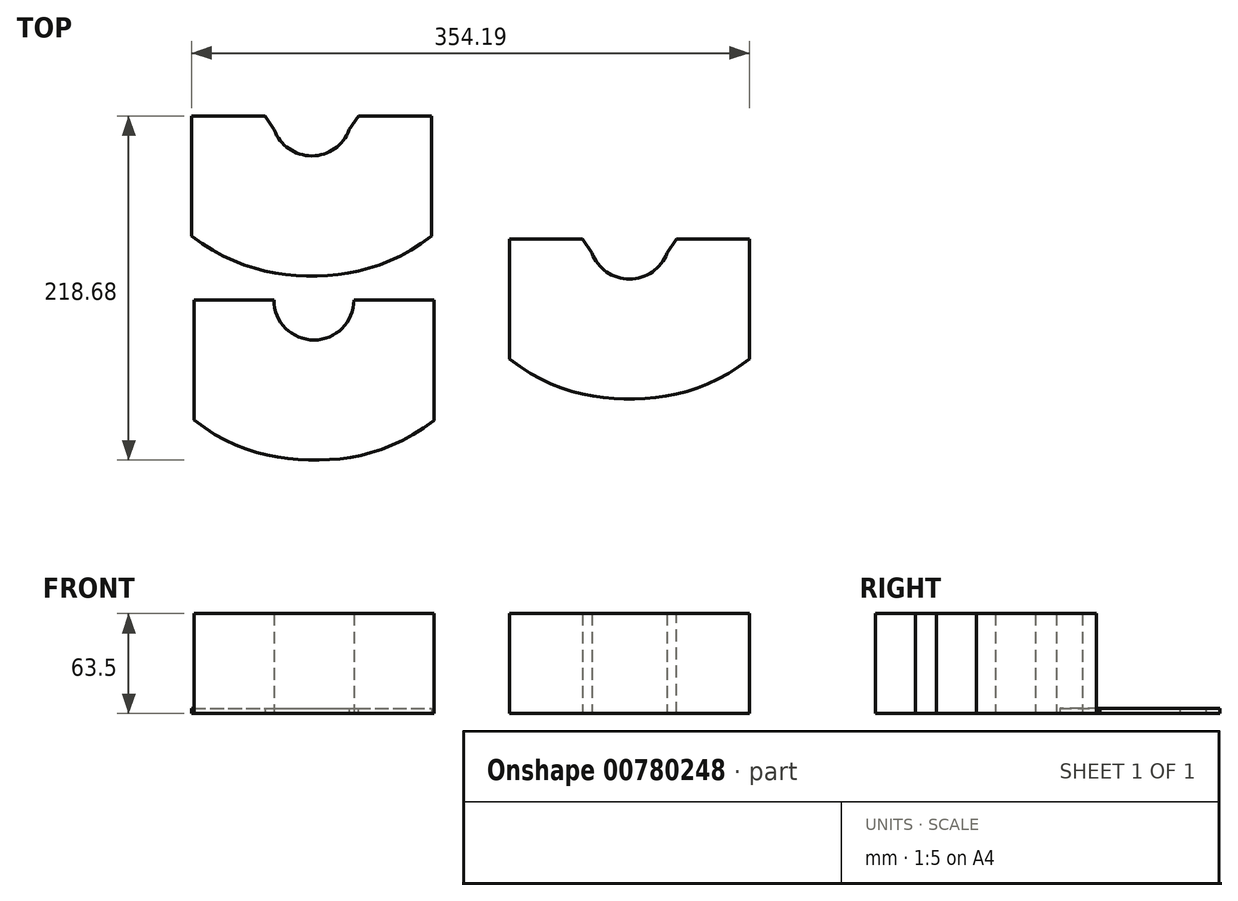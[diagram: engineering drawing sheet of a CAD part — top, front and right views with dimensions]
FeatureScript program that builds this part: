
annotation { "Feature Type Name" : "Feature", "Feature Type Description" : "" }
export const myFeature = defineFeature(function(context is Context, id is Id, definition is map)
    precondition{}
    {
        {
            var Q0;
            Q0=qCreatedBy(makeId("Top.planeOp"),FACE);
            var sketch = newSketch(context, id + "F0", { "sketchPlane" : qUnion([Q0])});
            skLineSegment(sketch, "E0.bottom", {"start": v(-76.2, 25.4) * mm, "end": v(-50.8, 25.4) * mm});
            skLineSegment(sketch, "E0.top", {"start": v(-70.9, -50.8) * mm, "end": v(-50.8, -50.8) * mm});
            skLineSegment(sketch, "E0.left", {"start": v(-76.2, 25.4) * mm, "end": v(-76.2, -50.8) * mm});
            skLineSegment(sketch, "E0.right", {"start": v(-50.8, 22.22) * mm, "end": v(-50.8, -50.8) * mm});
            skLineSegment(sketch, "E1.bottom", {"start": v(50.8, 25.4) * mm, "end": v(76.2, 25.4) * mm});
            skLineSegment(sketch, "E1.top", {"start": v(50.8, -50.98) * mm, "end": v(70.9, -50.98) * mm});
            skLineSegment(sketch, "E1.left", {"start": v(50.8, 22.22) * mm, "end": v(50.8, -50.98) * mm});
            skLineSegment(sketch, "E1.right", {"start": v(76.2, 25.4) * mm, "end": v(76.2, -50.98) * mm});
            skLineSegment(sketch, "E2.bottom", {"start": v(-50.8, 25.4) * mm, "end": v(-25.4, 25.4) * mm});
            skLineSegment(sketch, "E2.top", {"start": v(-50.8, 0) * mm, "end": v(-28.57, 0) * mm});
            skLineSegment(sketch, "E2.left", {"start": v(-50.8, 22.22) * mm, "end": v(-50.8, 0) * mm});
            skLineSegment(sketch, "E2.right", {"start": v(-25.4, 25.4) * mm, "end": v(-25.4, 25.4) * mm});
            skLineSegment(sketch, "E3.bottom", {"start": v(50.8, 25.4) * mm, "end": v(25.4, 25.4) * mm});
            skLineSegment(sketch, "E3.top", {"start": v(50.8, 0) * mm, "end": v(28.58, 0) * mm});
            skLineSegment(sketch, "E3.left", {"start": v(50.8, 22.22) * mm, "end": v(50.8, 0) * mm});
            skLineSegment(sketch, "E3.right", {"start": v(25.4, 25.4) * mm, "end": v(25.4, 25.4) * mm});
            skLineSegment(sketch, "E4", {"start": v(0, 0) * mm, "end": v(0, 0) * mm});
            skLineSegment(sketch, "E5", {"start": v(-50.8, -50.8) * mm, "end": v(50.8, -50.98) * mm, "construction": true});
            skFitSpline(sketch, "E6", {"points": [v(-76.2, -50.8) * mm, v(0, -76.3) * mm, v(76.2, -50.98) * mm], "startDerivative": vector(152.37, -117.67) * mm, "endDerivative": vector(152.4, 117.72) * mm});
            skLineSegment(sketch, "E7", {"start": v(0, -50.9) * mm, "end": v(0, -76.3) * mm, "construction": true});
            skLineSegment(sketch, "E8", {"start": v(50.8, -50.98) * mm, "end": v(50.8, -70.6) * mm, "construction": true});
            skLineSegment(sketch, "E9", {"start": v(-50.8, -50.8) * mm, "end": v(-50.8, -70.42) * mm, "construction": true});
            skLineSegment(sketch, "E10.0", {"start": v(-73.02, 22.23) * mm, "end": v(-50.8, 22.23) * mm});
            skLineSegment(sketch, "E10.1", {"start": v(-50.8, 22.23) * mm, "end": v(-28.57, 22.23) * mm});
            skLineSegment(sketch, "E10.2", {"start": v(-73.02, 22.22) * mm, "end": v(-73.02, -49.23) * mm});
            skLineSegment(sketch, "E10.3", {"start": v(-28.57, 22.22) * mm, "end": v(-28.57, 22.22) * mm});
            skLineSegment(sketch, "E10.4", {"start": v(-3.17, -3.17) * mm, "end": v(3.18, -3.17) * mm});
            skLineSegment(sketch, "E10.5", {"start": v(28.58, 22.22) * mm, "end": v(28.58, 22.23) * mm});
            skFitSpline(sketch, "E10.6", {"points": [v(-74.26, -48.29) * mm, v(-68.05, -53.08) * mm, v(-55.68, -60.96) * mm, v(-40.26, -67.2) * mm, v(-27.92, -70.4) * mm, v(-18.64, -72.02) * mm, v(-10.9, -72.77) * mm, v(-4.68, -73.06) * mm, v(0, -73.14) * mm, v(4.66, -73.08) * mm, v(10.88, -72.81) * mm, v(18.63, -72.09) * mm, v(27.9, -70.5) * mm, v(40.25, -67.33) * mm, v(55.67, -61.13) * mm, v(68.05, -53.27) * mm, v(74.26, -48.47) * mm]});
            skLineSegment(sketch, "E10.7", {"start": v(73.02, 22.22) * mm, "end": v(73.02, -49.41) * mm});
            skLineSegment(sketch, "E10.8", {"start": v(50.8, 22.23) * mm, "end": v(73.02, 22.23) * mm});
            skLineSegment(sketch, "E10.9", {"start": v(50.8, 22.23) * mm, "end": v(28.58, 22.23) * mm});
            skPoint(sketch, "E11.visualSharp", {"position": v(-25.4, 0) * mm});
            skArc(sketch, "E11.filletArc", {"start": v(-25.4, 25.4) * mm, "mid": v(-17.96, 7.44) * mm, "end": v(0, 0) * mm});
            skPoint(sketch, "E12.visualSharp", {"position": v(25.4, 0) * mm});
            skArc(sketch, "E12.filletArc", {"start": v(0, 0) * mm, "mid": v(17.96, 7.44) * mm, "end": v(25.4, 25.4) * mm});
            skPoint(sketch, "E13.visualSharp", {"position": v(-28.57, -3.18) * mm});
            skArc(sketch, "E13.filletArc", {"start": v(-28.57, 22.22) * mm, "mid": v(-21.14, 4.26) * mm, "end": v(-3.17, -3.18) * mm});
            skPoint(sketch, "E14.visualSharp", {"position": v(28.58, -3.18) * mm});
            skArc(sketch, "E14.filletArc", {"start": v(3.18, -3.17) * mm, "mid": v(21.14, 4.26) * mm, "end": v(28.58, 22.23) * mm});
            skSolve(sketch);
        }
        {
            var Q0;
            Q0=qCreatedBy(makeId("Top.planeOp"),FACE);
            var sketch = newSketch(context, id + "F1", { "sketchPlane" : qUnion([Q0])});
            skLineSegment(sketch, "E15.bottom", {"start": v(-77.6, 142.4) * mm, "end": v(-52.2, 142.4) * mm});
            skLineSegment(sketch, "E15.left", {"start": v(-77.6, 142.4) * mm, "end": v(-77.6, 66.2) * mm});
            skLineSegment(sketch, "E16.bottom", {"start": v(49.4, 142.4) * mm, "end": v(74.8, 142.4) * mm});
            skLineSegment(sketch, "E16.right", {"start": v(74.8, 142.4) * mm, "end": v(74.8, 66.2) * mm});
            skLineSegment(sketch, "E17.bottom", {"start": v(-52.2, 142.4) * mm, "end": v(-26.8, 142.4) * mm});
            skLineSegment(sketch, "E17.right", {"start": v(-26.8, 142.4) * mm, "end": v(-26.8, 142.4) * mm});
            skLineSegment(sketch, "E18.bottom", {"start": v(49.4, 142.4) * mm, "end": v(24, 142.4) * mm});
            skLineSegment(sketch, "E18.right", {"start": v(24, 142.4) * mm, "end": v(24, 142.4) * mm});
            skLineSegment(sketch, "E19", {"start": v(-1.4, 117) * mm, "end": v(-1.4, 117) * mm});
            skFitSpline(sketch, "E20", {"points": [v(-77.6, 66.2) * mm, v(-1.4, 40.8) * mm, v(74.8, 66.2) * mm], "startDerivative": vector(152.4, -117.7) * mm, "endDerivative": vector(152.4, 117.7) * mm});
            skPoint(sketch, "E21.visualSharp", {"position": v(-26.8, 117) * mm});
            skArc(sketch, "E21.filletArc", {"start": v(-26.8, 142.4) * mm, "mid": v(-19.36, 124.43) * mm, "end": v(-1.4, 117) * mm});
            skPoint(sketch, "E22.visualSharp", {"position": v(24, 117) * mm});
            skArc(sketch, "E22.filletArc", {"start": v(-1.4, 117) * mm, "mid": v(16.56, 124.43) * mm, "end": v(24, 142.4) * mm});
            skLineSegment(sketch, "E23", {"start": v(-26.8, 142.4) * mm, "end": v(24, 142.4) * mm, "construction": true});
            skSolve(sketch);
        }
        {
            var Q0;
            Q0=makeQuery(id+"F0.imprint","IMPRINT",FACE,{"disambiguationData":[TD([[makeQuery(id+"F0.imprint","IMPRINT",EDGE,{"derivedFrom":sQuery(id+"F0.wireOp",EDGE,"E0.bottom")}),-1.0]])]});
            extrude(context, id + "F2", {"entities" : qUnion([Q0]), "depth" : 63.5 * mm, "offsetDistance" : 25.4 * mm});
        }
        {
            var Q0;
            Q0=makeQuery(id+"F1.imprint","IMPRINT",FACE,{"disambiguationData":[TD([[makeQuery(id+"F1.imprint","IMPRINT",EDGE,{"derivedFrom":sQuery(id+"F1.wireOp",EDGE,"E15.bottom")}),-1.0]])]});
            extrude(context, id + "F3", {"entities" : qUnion([Q0]), "depth" : 3.17 * mm, "offsetDistance" : 25.4 * mm});
        }
        {
            var Q0;
            Q0=makeQuery(id+"F3.opExtrude","SWEPT_EDGE",EDGE,{"disambiguationData":[OSD([sQuery(id+"F1.wireOp",EDGE,"E17.bottom"),sQuery(id+"F1.wireOp",EDGE,"E21.filletArc")])]});
            var Q1;
            Q1=makeQuery(id+"F3.opExtrude","SWEPT_EDGE",EDGE,{"disambiguationData":[OSD([sQuery(id+"F1.wireOp",EDGE,"E18.bottom"),sQuery(id+"F1.wireOp",EDGE,"E22.filletArc")])]});
            chamfer(context, id + "F4", {"entities" : qUnion([Q0, Q1]), "chamferType" : ChamferType.OFFSET_ANGLE, "width" : 6.35 * mm, "oppositeDirection" : false, "angle" : 60 * degree, "tangentPropagation" : true});
        }
        {
            var Q0;
            Q0=qCreatedBy(makeId("Top.planeOp"),FACE);
            var sketch = newSketch(context, id + "F5", { "sketchPlane" : qUnion([Q0])});
            skLineSegment(sketch, "E24.bottom", {"start": v(124.2, 64.1) * mm, "end": v(149.6, 64.1) * mm});
            skLineSegment(sketch, "E24.left", {"start": v(124.2, 64.1) * mm, "end": v(124.2, -12.1) * mm});
            skLineSegment(sketch, "E25.bottom", {"start": v(251.2, 64.1) * mm, "end": v(276.6, 64.1) * mm});
            skLineSegment(sketch, "E25.right", {"start": v(276.6, 64.1) * mm, "end": v(276.6, -12.1) * mm});
            skLineSegment(sketch, "E26.bottom", {"start": v(149.6, 64.1) * mm, "end": v(175, 64.1) * mm});
            skLineSegment(sketch, "E26.right", {"start": v(175, 64.1) * mm, "end": v(175, 64.1) * mm});
            skLineSegment(sketch, "E27.bottom", {"start": v(251.2, 64.1) * mm, "end": v(225.8, 64.1) * mm});
            skLineSegment(sketch, "E27.right", {"start": v(225.8, 64.1) * mm, "end": v(225.8, 64.1) * mm});
            skLineSegment(sketch, "E28", {"start": v(200.4, 38.7) * mm, "end": v(200.4, 38.7) * mm});
            skFitSpline(sketch, "E29", {"points": [v(124.2, -12.1) * mm, v(200.4, -37.5) * mm, v(276.6, -12.1) * mm], "startDerivative": vector(152.4, -117.7) * mm, "endDerivative": vector(152.4, 117.7) * mm});
            skPoint(sketch, "E30.visualSharp", {"position": v(175, 38.7) * mm});
            skArc(sketch, "E30.filletArc", {"start": v(175, 64.1) * mm, "mid": v(182.43, 46.13) * mm, "end": v(200.4, 38.7) * mm});
            skPoint(sketch, "E31.visualSharp", {"position": v(225.8, 38.7) * mm});
            skArc(sketch, "E31.filletArc", {"start": v(200.4, 38.7) * mm, "mid": v(218.35, 46.13) * mm, "end": v(225.8, 64.1) * mm});
            skLineSegment(sketch, "E32", {"start": v(175, 64.1) * mm, "end": v(225.8, 64.1) * mm, "construction": true});
            skLineSegment(sketch, "E33.0", {"start": v(127.37, 60.92) * mm, "end": v(149.6, 60.92) * mm});
            skLineSegment(sketch, "E33.1", {"start": v(149.6, 60.92) * mm, "end": v(172, 60.92) * mm});
            skLineSegment(sketch, "E33.2", {"start": v(127.37, 60.92) * mm, "end": v(127.37, -10.54) * mm});
            skArc(sketch, "E33.3", {"start": v(172, 60.92) * mm, "mid": v(181.34, 42.8) * mm, "end": v(200.4, 35.52) * mm});
            skArc(sketch, "E33.4", {"start": v(200.4, 35.52) * mm, "mid": v(219.44, 42.8) * mm, "end": v(228.8, 60.92) * mm});
            skFitSpline(sketch, "E33.5", {"points": [v(126.13, -9.6) * mm, v(132.34, -14.39) * mm, v(144.72, -22.26) * mm, v(160.14, -28.48) * mm, v(172.48, -31.67) * mm, v(181.76, -33.27) * mm, v(189.51, -34) * mm, v(195.72, -34.29) * mm, v(200.4, -34.35) * mm, v(205.06, -34.29) * mm, v(211.28, -34) * mm, v(219.03, -33.27) * mm, v(228.3, -31.67) * mm, v(240.65, -28.48) * mm, v(256.07, -22.26) * mm, v(268.45, -14.39) * mm, v(274.65, -9.6) * mm]});
            skLineSegment(sketch, "E33.6", {"start": v(273.42, 60.92) * mm, "end": v(273.42, -10.54) * mm});
            skLineSegment(sketch, "E33.7", {"start": v(251.2, 60.92) * mm, "end": v(273.42, 60.92) * mm});
            skLineSegment(sketch, "E33.8", {"start": v(251.2, 60.92) * mm, "end": v(228.8, 60.92) * mm});
            skSolve(sketch);
        }
        {
            var Q0;
            Q0=makeQuery(id+"F5.imprint","IMPRINT",FACE,{"disambiguationData":[TD([[makeQuery(id+"F5.imprint","IMPRINT",EDGE,{"derivedFrom":sQuery(id+"F5.wireOp",EDGE,"ad2a8b3e-1aac-4135-8621-85bd7044a372.bottom")}),-1.0]])]});
            var Q1;
            Q1=makeQuery(id+"F5.imprint","IMPRINT",FACE,{"disambiguationData":[TD([[makeQuery(id+"F5.imprint","IMPRINT",EDGE,{"derivedFrom":sQuery(id+"F5.wireOp",EDGE,"E24.bottom")}),-1.0]])]});
            extrude(context, id + "F6", {"entities" : qUnion([Q0, Q1]), "depth" : 63.5 * mm, "offsetDistance" : 25.4 * mm});
        }
        {
            var Q0;
            Q0=makeQuery(id+"F6.opExtrude","SWEPT_EDGE",EDGE,{"disambiguationData":[OSD([sQuery(id+"F5.wireOp",EDGE,"E26.bottom"),sQuery(id+"F5.wireOp",EDGE,"E30.filletArc")])]});
            var Q1;
            Q1=makeQuery(id+"F6.opExtrude","SWEPT_EDGE",EDGE,{"disambiguationData":[OSD([sQuery(id+"F5.wireOp",EDGE,"E27.bottom"),sQuery(id+"F5.wireOp",EDGE,"E31.filletArc")])]});
            chamfer(context, id + "F7", {"entities" : qUnion([Q0, Q1]), "chamferType" : ChamferType.OFFSET_ANGLE, "width" : 6.35 * mm, "oppositeDirection" : false, "angle" : 60 * degree, "tangentPropagation" : true});
        }
    });
